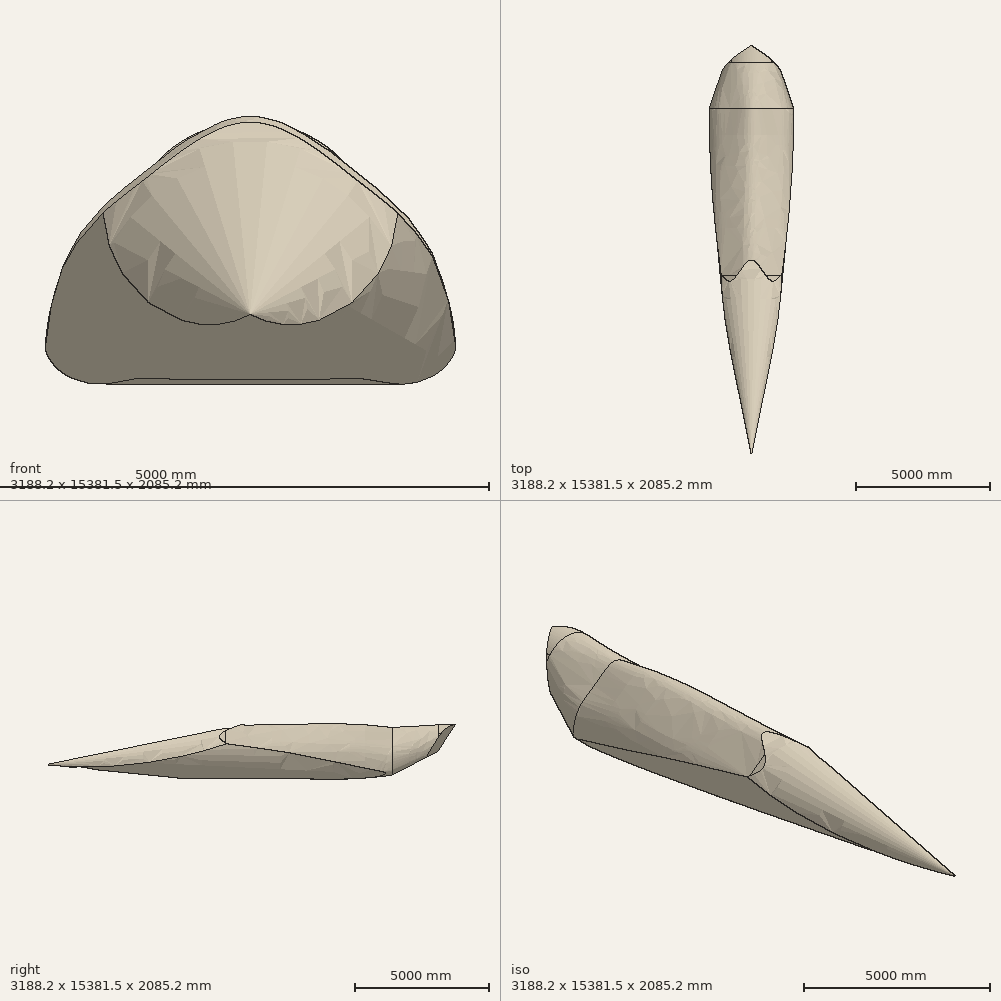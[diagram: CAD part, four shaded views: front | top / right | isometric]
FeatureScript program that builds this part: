
annotation { "Feature Type Name" : "Feature", "Feature Type Description" : "" }
export const myFeature = defineFeature(function(context is Context, id is Id, definition is map)
    precondition{}
    {
        {
            var Q0;
            Q0=qCreatedBy(makeId("Front.planeOp"),FACE);
            cPlane(context, id + "F0", {"entities" : qUnion([Q0]), "cplaneType" : CPlaneType.OFFSET, "offset" : 1750 * mm, "width" : 152.4 * mm, "height" : 152.4 * mm});
        }
        {
            var Q0;
            Q0=qCreatedBy(id+"F0.planeOp",FACE);
            var sketch = newSketch(context, id + "F1", { "sketchPlane" : qUnion([Q0])});
            skLineSegment(sketch, "E0.top", {"start": v(-1394.2, -1000) * mm, "end": v(1394.2, -1000) * mm});
            skPoint(sketch, "E0.middle", {"position": v(0, 0) * mm});
            skFitSpline(sketch, "E1", {"points": [v(-1600, -1000) * mm, v(-848, 530) * mm, v(0, 1000) * mm, v(848, 530) * mm, v(1600, -1000) * mm], "startDerivative": vector(0, 10524.75) * mm, "endDerivative": vector(0, -10524.75) * mm});
            skArc(sketch, "E2.filletArc", {"start": v(-1593.82, -787.83) * mm, "mid": v(-1539.85, -937.05) * mm, "end": v(-1394.2, -1000) * mm});
            skArc(sketch, "E3.filletArc", {"start": v(1394.2, -1000) * mm, "mid": v(1539.85, -937.05) * mm, "end": v(1593.82, -787.83) * mm});
            skSolve(sketch);
        }
        {
            var Q0;
            Q0=qCreatedBy(makeId("Front.planeOp"),FACE);
            var sketch = newSketch(context, id + "F2", { "sketchPlane" : qUnion([Q0])});
            skLineSegment(sketch, "E4.top", {"start": v(-1394.2, -1000) * mm, "end": v(1394.2, -1000) * mm});
            skPoint(sketch, "E4.middle", {"position": v(0, 0) * mm});
            skFitSpline(sketch, "E5", {"points": [v(-1600, -1000) * mm, v(-848, 530) * mm, v(0, 1000) * mm, v(848, 530) * mm, v(1600, -1000) * mm], "startDerivative": vector(0, 10524.75) * mm, "endDerivative": vector(0, -10524.75) * mm});
            skArc(sketch, "E6.filletArc", {"start": v(-1593.82, -787.83) * mm, "mid": v(-1539.85, -937.05) * mm, "end": v(-1394.2, -1000) * mm});
            skArc(sketch, "E7.filletArc", {"start": v(1394.2, -1000) * mm, "mid": v(1539.85, -937.05) * mm, "end": v(1593.82, -787.83) * mm});
            skSolve(sketch);
        }
        {
            var Q0;
            Q0=qCreatedBy(makeId("Front.planeOp"),FACE);
            cPlane(context, id + "F3", {"entities" : qUnion([Q0]), "cplaneType" : CPlaneType.OFFSET, "offset" : 3500 * mm, "oppositeDirection" : true, "width" : 150 * mm, "height" : 150 * mm});
        }
        {
            var Q0;
            Q0=qCreatedBy(id+"F3.planeOp",FACE);
            var sketch = newSketch(context, id + "F4", { "sketchPlane" : qUnion([Q0])});
            skLineSegment(sketch, "E8.top", {"start": v(-1394.2, -1000) * mm, "end": v(1394.2, -1000) * mm});
            skPoint(sketch, "E8.middle", {"position": v(0, 0) * mm});
            skFitSpline(sketch, "E9", {"points": [v(-1600, -1000) * mm, v(-848, 530) * mm, v(0, 1000) * mm, v(848, 530) * mm, v(1600, -1000) * mm], "startDerivative": vector(0, 10524.75) * mm, "endDerivative": vector(0, -10524.75) * mm});
            skArc(sketch, "E10.filletArc", {"start": v(-1593.82, -787.83) * mm, "mid": v(-1539.85, -937.05) * mm, "end": v(-1394.2, -1000) * mm});
            skArc(sketch, "E11.filletArc", {"start": v(1394.2, -1000) * mm, "mid": v(1539.85, -937.05) * mm, "end": v(1593.82, -787.83) * mm});
            skSolve(sketch);
        }
        {
            var Q0;
            Q0=qCreatedBy(makeId("Front.planeOp"),FACE);
            cPlane(context, id + "F5", {"entities" : qUnion([Q0]), "cplaneType" : CPlaneType.OFFSET, "offset" : 4500 * mm, "oppositeDirection" : true, "width" : 150 * mm, "height" : 150 * mm});
        }
        {
            var Q0;
            Q0=qCreatedBy(id+"F5.planeOp",FACE);
            var sketch = newSketch(context, id + "F6", { "sketchPlane" : qUnion([Q0])});
            skLineSegment(sketch, "E12.top", {"start": v(-1413.07, -900) * mm, "end": v(1413.07, -900) * mm});
            skPoint(sketch, "E12.middle", {"position": v(0, 0) * mm});
            skFitSpline(sketch, "E13", {"points": [v(-1600, -900) * mm, v(-784.42, 441.24) * mm, v(0, 900) * mm, v(784.42, 441.24) * mm, v(1600, -900) * mm], "startDerivative": vector(0, 9508.62) * mm, "endDerivative": vector(0, -9508.62) * mm});
            skArc(sketch, "E14.filletArc", {"start": v(-1592.48, -705.43) * mm, "mid": v(-1545.4, -842.02) * mm, "end": v(-1413.07, -900) * mm});
            skArc(sketch, "E15.filletArc", {"start": v(1413.07, -900) * mm, "mid": v(1545.4, -842.02) * mm, "end": v(1592.48, -705.43) * mm});
            skSolve(sketch);
        }
        {
            var Q0;
            Q0=qCreatedBy(makeId("Front.planeOp"),FACE);
            cPlane(context, id + "F7", {"entities" : qUnion([Q0]), "cplaneType" : CPlaneType.OFFSET, "offset" : 6232.05 * mm, "oppositeDirection" : true, "width" : 150 * mm, "height" : 150 * mm});
        }
        {
            var Q0;
            Q0=qCreatedBy(id+"F7.planeOp",FACE);
            var sketch = newSketch(context, id + "F8", { "sketchPlane" : qUnion([Q0])});
            skArc(sketch, "E16", {"start": v(998.61, 52.63) * mm, "mid": v(0, 1000) * mm, "end": v(-998.61, 52.63) * mm});
            skLineSegment(sketch, "E17", {"start": v(0, 0) * mm, "end": v(-948.68, 0) * mm});
            skLineSegment(sketch, "E18", {"start": v(0, 0) * mm, "end": v(948.68, 0) * mm});
            skPoint(sketch, "E19.visualSharp", {"position": v(-1000, 0) * mm});
            skArc(sketch, "E19.filletArc", {"start": v(-998.61, 52.63) * mm, "mid": v(-984.96, 15.59) * mm, "end": v(-948.68, 0) * mm});
            skPoint(sketch, "E20.visualSharp", {"position": v(1000, 0) * mm});
            skArc(sketch, "E20.filletArc", {"start": v(948.68, 0) * mm, "mid": v(984.96, 15.59) * mm, "end": v(998.61, 52.63) * mm});
            skLineSegment(sketch, "E21", {"start": v(0, 1000) * mm, "end": v(0, 675) * mm, "construction": true});
            skPoint(sketch, "E21.endSnap0", {"position": v(0, 1000) * mm});
            skLineSegment(sketch, "E22", {"start": v(0, 675) * mm, "end": v(737.82, 675) * mm, "construction": true});
            skLineSegment(sketch, "E23", {"start": v(0, 675) * mm, "end": v(-737.82, 675) * mm, "construction": true});
            skSolve(sketch);
        }
        {
            var Q0;
            Q0=sQuery(id+"F8.wireOp",EDGE,"E23");
            var Q1;
            Q1=sQuery(id+"F6.wireOp",VERTEX,"E13.1.internal");
            cPlane(context, id + "F9", {"entities" : qUnion([Q0, Q1]), "cplaneType" : CPlaneType.LINE_ANGLE, "offset" : 25 * mm, "angle" : 0 * degree, "width" : 150 * mm, "height" : 150 * mm});
        }
        {
            var Q0;
            Q0=qCreatedBy(id+"F9.planeOp",FACE);
            var sketch = newSketch(context, id + "F10", { "sketchPlane" : qUnion([Q0])});
            skLineSegment(sketch, "E24", {"start": v(-784.42, 4518.58) * mm, "end": v(-737.82, 6266.34) * mm});
            skLineSegment(sketch, "E25", {"start": v(784.42, 4518.58) * mm, "end": v(737.82, 6266.34) * mm});
            skSolve(sketch);
        }
        {
            var Q0;
            Q0=makeQuery(id+"F1.imprint","IMPRINT",FACE,{"disambiguationData":[TD([[makeQuery(id+"F1.imprint","IMPRINT",EDGE,{"derivedFrom":sQuery(id+"F1.wireOp",EDGE,"E0.top")}),1.0]])]});
            var Q1;
            Q1=makeQuery(id+"F2.imprint","IMPRINT",FACE,{"disambiguationData":[TD([[makeQuery(id+"F2.imprint","IMPRINT",EDGE,{"derivedFrom":sQuery(id+"F2.wireOp",EDGE,"E4.top")}),1.0]])]});
            var Q2;
            Q2=makeQuery(id+"F4.imprint","IMPRINT",FACE,{"disambiguationData":[TD([[makeQuery(id+"F4.imprint","IMPRINT",EDGE,{"derivedFrom":sQuery(id+"F4.wireOp",EDGE,"E8.top")}),1.0]])]});
            var Q3;
            Q3=makeQuery(id+"F6.imprint","IMPRINT",FACE,{"disambiguationData":[TD([[makeQuery(id+"F6.imprint","IMPRINT",EDGE,{"derivedFrom":sQuery(id+"F6.wireOp",EDGE,"E12.top")}),1.0]])]});
            loft(context, id + "F11", {"sheetProfilesArray" : [{ "sheetProfileEntities" : qUnion([Q0]) }, { "sheetProfileEntities" : qUnion([Q1]) }, { "sheetProfileEntities" : qUnion([Q2]) }, { "sheetProfileEntities" : qUnion([Q3]) }]});
        }
        {
            var Q1;
            Q1=makeQuery(id+"F6.imprint","IMPRINT",FACE,{"disambiguationData":[TD([[makeQuery(id+"F6.imprint","IMPRINT",EDGE,{"derivedFrom":sQuery(id+"F6.wireOp",EDGE,"E12.top")}),1.0]])]});
            var Q2;
            Q2=makeQuery(id+"F8.imprint","IMPRINT",FACE,{"disambiguationData":[TD([[makeQuery(id+"F8.imprint","IMPRINT",EDGE,{"derivedFrom":sQuery(id+"F8.wireOp",EDGE,"E16")}),1.0]])]});
            var Q3;
            Q3=sQuery(id+"F10.wireOp",EDGE,"E24");
            var Q4;
            Q4=sQuery(id+"F10.wireOp",EDGE,"E25");
            loft(context, id + "F12", {"operationType" : NewBodyOperationType.ADD, "addGuides" : true, "sheetProfilesArray" : [{ "sheetProfileEntities" : qUnion([Q1]) }, { "sheetProfileEntities" : qUnion([Q2]) }], "guidesArray" : [{ "guideEntities" : qUnion([Q3]), "guideDerivativeType" : LoftGuideDerivativeType.DEFAULT, "guideDerivativeMagnitude" : 1 }, { "guideEntities" : qUnion([Q4]), "guideDerivativeType" : LoftGuideDerivativeType.DEFAULT, "guideDerivativeMagnitude" : 1 }]});
        }
        {
            var Q0;
            Q0=makeQuery(id+"F11.opLoft","CAP_FACE",FACE,{"disambiguationData":[OSD([makeQuery(id+"F1.imprint","IMPRINT",FACE,{"disambiguationData":[TD([[makeQuery(id+"F1.imprint","IMPRINT",EDGE,{"derivedFrom":sQuery(id+"F1.wireOp",EDGE,"E0.top")}),1.0]])]})])],"isStart":true});
            extrude(context, id + "F13", {"entities" : qUnion([Q0]), "operationType" : NewBodyOperationType.ADD, "depth" : 6750 * mm});
        }
        {
            var Q0;
            Q0=qCreatedBy(makeId("Right.planeOp"),FACE);
            var sketch = newSketch(context, id + "F14", { "sketchPlane" : qUnion([Q0])});
            skLineSegment(sketch, "E26", {"start": v(0, 0) * mm, "end": v(-3500, 0) * mm});
            skLineSegment(sketch, "E27", {"start": v(-3500, 0) * mm, "end": v(-3500, -1000) * mm});
            skLineSegment(sketch, "E28", {"start": v(-3500, -1000) * mm, "end": v(-8500, -1000) * mm});
            skLineSegment(sketch, "E29", {"start": v(-8500, -1000) * mm, "end": v(-8500, -499.31) * mm});
            skLineSegment(sketch, "E30", {"start": v(-1151.4, 0) * mm, "end": v(-1151.4, 1000) * mm});
            skLineSegment(sketch, "E31", {"start": v(-1151.4, 1000) * mm, "end": v(-8500, -499.31) * mm});
            skLineSegment(sketch, "E32", {"start": v(-8500, -499.31) * mm, "end": v(-3500, -1000) * mm});
            skLineSegment(sketch, "E33", {"start": v(-1151.4, 1000) * mm, "end": v(-8500, 1000) * mm});
            skLineSegment(sketch, "E34", {"start": v(-8500, 1000) * mm, "end": v(-8500, -499.31) * mm});
            skLineSegment(sketch, "E35", {"start": v(-1750, 0) * mm, "end": v(-1750, -1000) * mm});
            skLineSegment(sketch, "E36", {"start": v(-1750, -1000) * mm, "end": v(-3500, -1000) * mm});
            skLineSegment(sketch, "E37", {"start": v(-8500, -1000) * mm, "end": v(-8500, -1980) * mm});
            skLineSegment(sketch, "E38", {"start": v(-3500, -1000) * mm, "end": v(6286.5, -1980) * mm});
            skLineSegment(sketch, "E39", {"start": v(-8500, -1980) * mm, "end": v(6286.5, -1980) * mm});
            skLineSegment(sketch, "E40", {"start": v(-8500, -499.31) * mm, "end": v(-3500, -499.31) * mm});
            skSolve(sketch);
        }
        {
            var Q0;
            Q0=makeQuery(id+"F14.imprint","IMPRINT",FACE,{"disambiguationData":[TD([[makeQuery(id+"F14.imprint","IMPRINT",EDGE,{"derivedFrom":sQuery(id+"F14.wireOp",EDGE,"E31")}),-1.0]])]});
            var Q1;
            Q1=sQuery(id+"F14.wireOp",EDGE,"E40");
            revolve(context, id + "F15", {"operationType" : NewBodyOperationType.REMOVE, "entities" : qUnion([Q0]), "axis" : qUnion([Q1]), "revolveType" : RevolveType.SYMMETRIC, "oppositeDirection" : true, "angle" : 250 * degree});
        }
        {
            var Q0;
            Q0=makeQuery(id+"F14.imprint","IMPRINT",FACE,{"disambiguationData":[TD([[makeQuery(id+"F14.imprint","IMPRINT",EDGE,{"derivedFrom":sQuery(id+"F14.wireOp",EDGE,"E28")}),-1.0]])]});
            var Q1;
            Q1=makeQuery(id+"F14.imprint","IMPRINT",FACE,{"disambiguationData":[TD([[makeQuery(id+"F14.imprint","IMPRINT",EDGE,{"derivedFrom":sQuery(id+"F14.wireOp",EDGE,"E28")}),1.0]])]});
            var Q2;
            Q2=sQuery(id+"F14.wireOp",EDGE,"E26");
            revolve(context, id + "F16", {"operationType" : NewBodyOperationType.REMOVE, "entities" : qUnion([Q0, Q1]), "axis" : qUnion([Q2]), "revolveType" : RevolveType.SYMMETRIC, "oppositeDirection" : true, "angle" : 240 * degree});
        }
        {
            var Q0;
            Q0=makeQuery(id+"F12.opLoft","CAP_FACE",FACE,{"disambiguationData":[OSD([makeQuery(id+"F8.imprint","IMPRINT",FACE,{"disambiguationData":[TD([[makeQuery(id+"F8.imprint","IMPRINT",EDGE,{"derivedFrom":sQuery(id+"F8.wireOp",EDGE,"E16")}),1.0]])]})])],"isStart":true});
            extrude(context, id + "F17", {"entities" : qUnion([Q0]), "operationType" : NewBodyOperationType.ADD, "depth" : 649.4 * mm});
        }
        {
            var Q0;
            Q0=qCreatedBy(makeId("Right.planeOp"),FACE);
            var sketch = newSketch(context, id + "F18", { "sketchPlane" : qUnion([Q0])});
            skLineSegment(sketch, "E41", {"start": v(0, 0) * mm, "end": v(4500, 0) * mm});
            skLineSegment(sketch, "E42", {"start": v(4500, 0) * mm, "end": v(6232.05, 0) * mm});
            skLineSegment(sketch, "E43", {"start": v(4500, 0) * mm, "end": v(4500, 1000) * mm});
            skLineSegment(sketch, "E44", {"start": v(4500, 1000) * mm, "end": v(6881.46, 1000) * mm});
            skLineSegment(sketch, "E45", {"start": v(6881.46, 1000) * mm, "end": v(6881.46, -1000) * mm});
            skLineSegment(sketch, "E46", {"start": v(6881.46, 1000) * mm, "end": v(6232.05, 0) * mm});
            skLineSegment(sketch, "E47", {"start": v(6232.05, 0) * mm, "end": v(5582.64, -1000) * mm});
            skLineSegment(sketch, "E48", {"start": v(5582.64, -1000) * mm, "end": v(6881.46, -1000) * mm});
            skSolve(sketch);
        }
        {
            var Q0;
            Q0=makeQuery(id+"F18.imprint","IMPRINT",FACE,{"disambiguationData":[TD([[makeQuery(id+"F18.imprint","IMPRINT",EDGE,{"derivedFrom":sQuery(id+"F18.wireOp",EDGE,"E45")}),-1.0]])]});
            var Q1;
            Q1=sQuery(id+"F18.wireOp",EDGE,"E44");
            revolve(context, id + "F19", {"operationType" : NewBodyOperationType.REMOVE, "entities" : qUnion([Q0]), "axis" : qUnion([Q1]), "revolveType" : RevolveType.SYMMETRIC, "oppositeDirection" : true, "angle" : 182 * degree});
        }
    });
